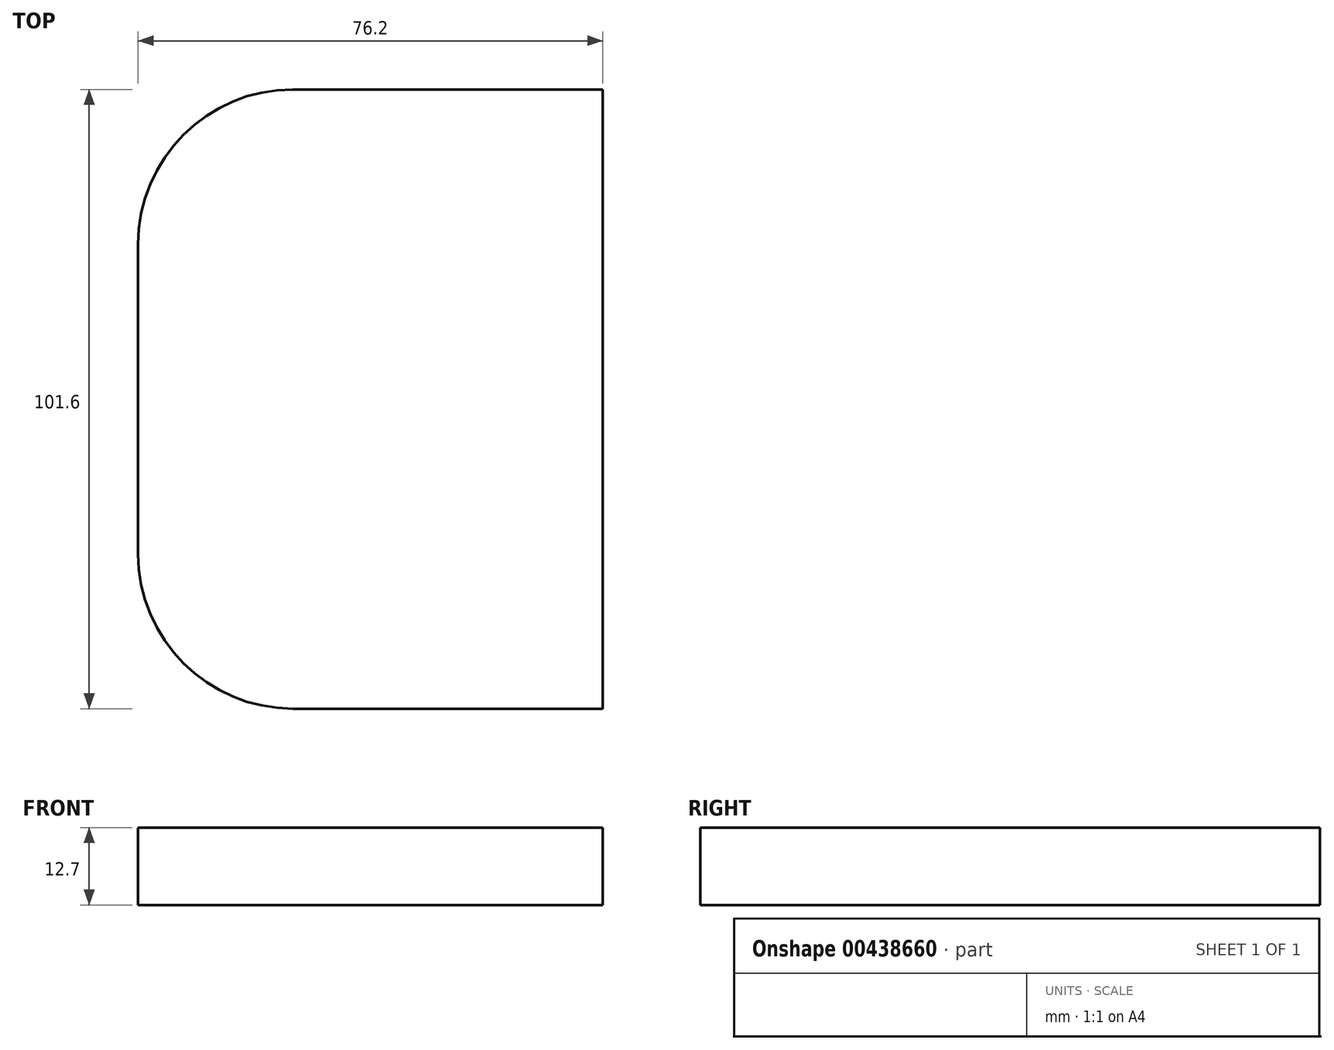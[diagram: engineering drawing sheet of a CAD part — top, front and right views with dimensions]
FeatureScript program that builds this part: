
annotation { "Feature Type Name" : "Feature", "Feature Type Description" : "" }
export const myFeature = defineFeature(function(context is Context, id is Id, definition is map)
    precondition{}
    {
        {
            var Q0;
            Q0=qCreatedBy(makeId("Top.planeOp"),FACE);
            var sketch = newSketch(context, id + "F0", { "sketchPlane" : qUnion([Q0])});
            skLineSegment(sketch, "E0.bottom", {"start": v(0, 0) * mm, "end": v(76.2, 0) * mm});
            skLineSegment(sketch, "E0.top", {"start": v(0, -101.6) * mm, "end": v(76.2, -101.6) * mm});
            skLineSegment(sketch, "E0.left", {"start": v(0, 0) * mm, "end": v(0, -101.6) * mm});
            skLineSegment(sketch, "E0.right", {"start": v(76.2, 0) * mm, "end": v(76.2, -101.6) * mm});
            skSolve(sketch);
        }
        {
            var Q0;
            Q0=makeQuery(id+"F0.imprint","IMPRINT",FACE,{"disambiguationData":[TD([[makeQuery(id+"F0.imprint","IMPRINT",EDGE,{"derivedFrom":sQuery(id+"F0.wireOp",EDGE,"E0.bottom")}),-1.0]])]});
            extrude(context, id + "F1", {"entities" : qUnion([Q0]), "oppositeDirection" : true, "depth" : 12.7 * mm});
        }
        {
            var Q0;
            Q0=makeQuery(id+"F1.opExtrude","SWEPT_EDGE",EDGE,{"disambiguationData":[OSD([sQuery(id+"F0.wireOp",EDGE,"E0.bottom"),sQuery(id+"F0.wireOp",EDGE,"E0.left")])]});
            var Q1;
            Q1=makeQuery(id+"F1.opExtrude","SWEPT_EDGE",EDGE,{"disambiguationData":[OSD([sQuery(id+"F0.wireOp",EDGE,"E0.top"),sQuery(id+"F0.wireOp",EDGE,"E0.left")])]});
            fillet(context, id + "F2", {"entities" : qUnion([Q0, Q1]), "radius" : 25.4 * mm, "tangentPropagation" : true, "allowEdgeOverflow" : false});
        }
        {
            var Q0;
            Q0=makeQuery(id+"F0.imprint","IMPRINT",FACE,{"disambiguationData":[TD([[makeQuery(id+"F0.imprint","IMPRINT",EDGE,{"derivedFrom":sQuery(id+"F0.wireOp",EDGE,"E0.bottom")}),-1.0]])]});
            cPlane(context, id + "F3", {"entities" : qUnion([Q0]), "cplaneType" : CPlaneType.OFFSET, "offset" : 0 * mm, "oppositeDirection" : true, "width" : 152.4 * mm, "height" : 152.4 * mm});
        }
    });
